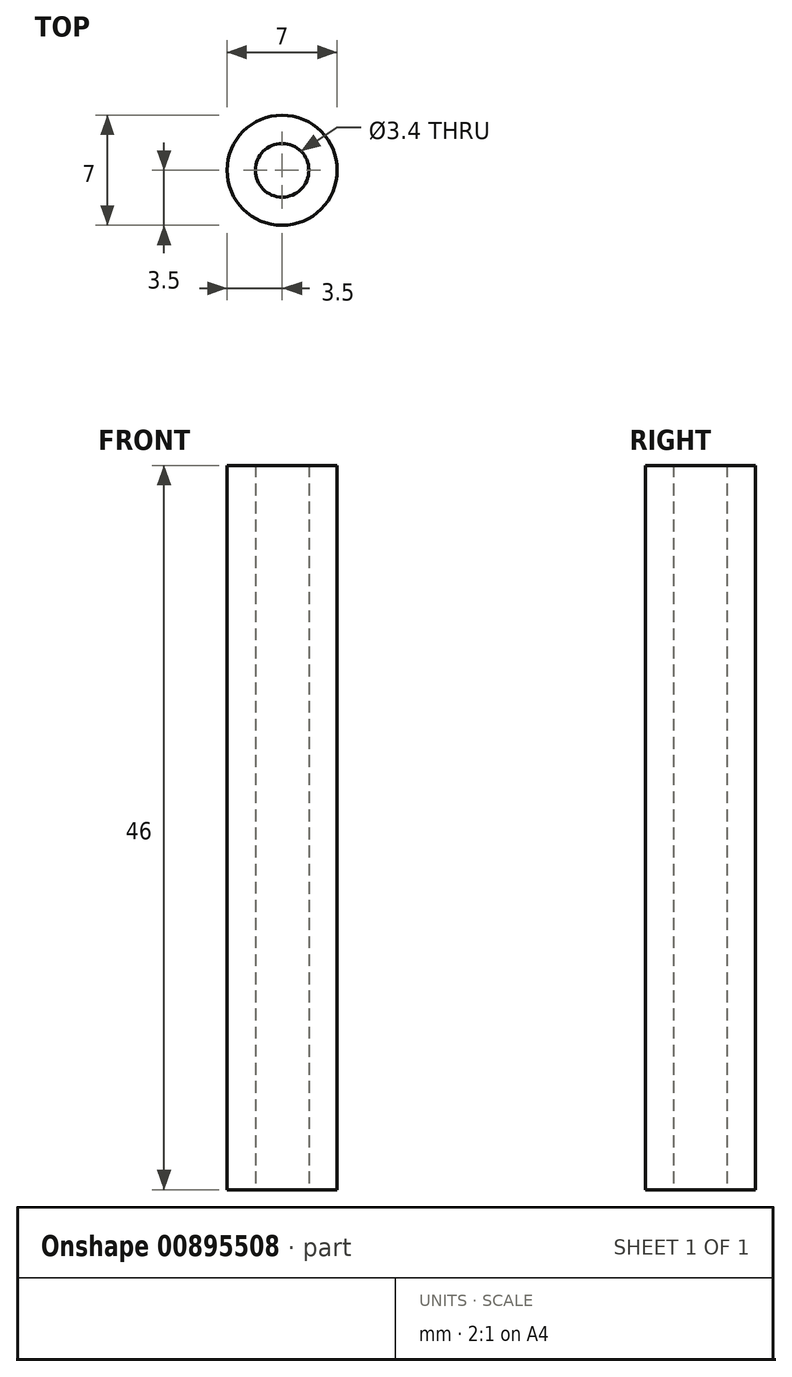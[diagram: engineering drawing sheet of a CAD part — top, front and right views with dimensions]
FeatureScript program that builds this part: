
annotation { "Feature Type Name" : "Feature", "Feature Type Description" : "" }
export const myFeature = defineFeature(function(context is Context, id is Id, definition is map)
    precondition{}
    {
        {
            var Q0;
            Q0=qCreatedBy(makeId("Top.planeOp"),FACE);
            var sketch = newSketch(context, id + "F0", { "sketchPlane" : qUnion([Q0])});
            skCircle(sketch, "E0", {"center": v(0, 0) * mm, "radius": 1.7 * mm});
            skCircle(sketch, "E1", {"center": v(0, 0) * mm, "radius": 3.5 * mm});
            skSolve(sketch);
        }
        {
            var Q0;
            Q0 = qSketchRegion(id + "F0", true);
            extrude(context, id + "F1", {"entities" : qUnion([Q0]), "depth" : 46 * mm, "offsetDistance" : 25 * mm});
        }
    });
